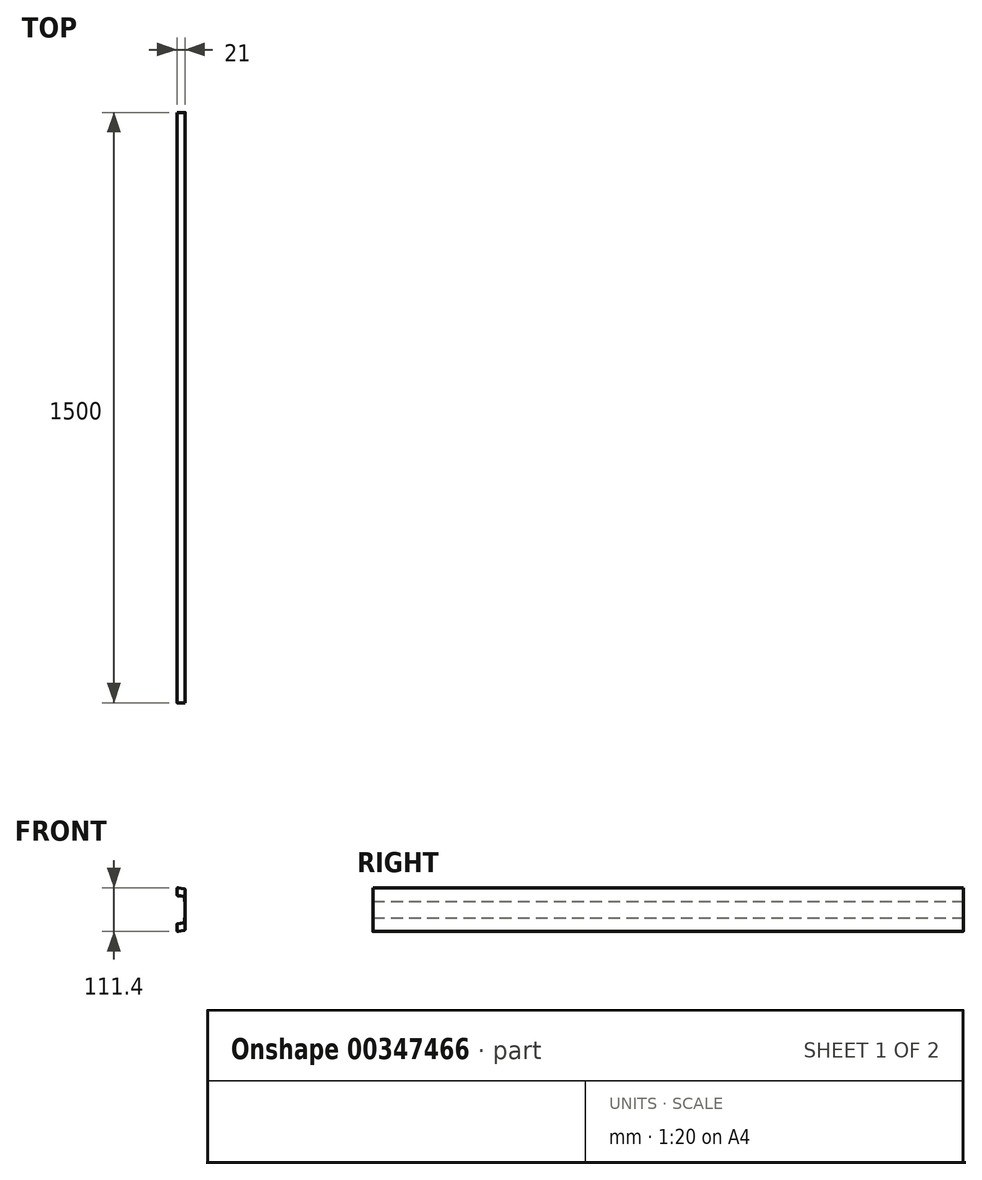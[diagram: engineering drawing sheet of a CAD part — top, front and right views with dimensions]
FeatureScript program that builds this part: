
annotation { "Feature Type Name" : "Feature", "Feature Type Description" : "" }
export const myFeature = defineFeature(function(context is Context, id is Id, definition is map)
    precondition{}
    {
        {
            var Q0;
            Q0=qCreatedBy(makeId("Front.planeOp"),FACE);
            var sketch = newSketch(context, id + "F0", { "sketchPlane" : qUnion([Q0])});
            skLineSegment(sketch, "E0", {"start": v(-1.5, -20.57) * mm, "end": v(-1.5, -32.53) * mm});
            skLineSegment(sketch, "E1", {"start": v(-1.5, -32.53) * mm, "end": v(-21, -35.97) * mm});
            skLineSegment(sketch, "E2", {"start": v(-21, -35.97) * mm, "end": v(-21, -56.27) * mm});
            skLineSegment(sketch, "E3", {"start": v(-21, -56.27) * mm, "end": v(0, -52.57) * mm});
            skLineSegment(sketch, "E4", {"start": v(0, -52.57) * mm, "end": v(0, 52.57) * mm});
            skLineSegment(sketch, "E5", {"start": v(0, 52.57) * mm, "end": v(-21, 56.27) * mm});
            skLineSegment(sketch, "E6", {"start": v(-21, 56.27) * mm, "end": v(-21, 35.97) * mm});
            skLineSegment(sketch, "E7", {"start": v(-21, 35.97) * mm, "end": v(-1.5, 32.53) * mm});
            skLineSegment(sketch, "E8", {"start": v(-1.5, 32.53) * mm, "end": v(-1.5, 20.57) * mm});
            skLineSegment(sketch, "E9.0", {"start": v(-1, 32.95) * mm, "end": v(-1, 20.57) * mm});
            skLineSegment(sketch, "E10.0", {"start": v(-20.5, 36.39) * mm, "end": v(-1, 32.95) * mm});
            skLineSegment(sketch, "E11.0", {"start": v(-20.5, 55.68) * mm, "end": v(-20.5, 36.39) * mm});
            skLineSegment(sketch, "E12.0", {"start": v(-0.5, 52.15) * mm, "end": v(-20.5, 55.68) * mm});
            skLineSegment(sketch, "E13.0", {"start": v(-0.5, -52.15) * mm, "end": v(-0.5, 52.15) * mm});
            skLineSegment(sketch, "E14.0", {"start": v(-20.5, -55.68) * mm, "end": v(-0.5, -52.15) * mm});
            skLineSegment(sketch, "E15.0", {"start": v(-20.5, -36.39) * mm, "end": v(-20.5, -55.68) * mm});
            skLineSegment(sketch, "E16.0", {"start": v(-1, -32.95) * mm, "end": v(-20.5, -36.39) * mm});
            skLineSegment(sketch, "E17.0", {"start": v(-1, -20.57) * mm, "end": v(-1, -32.95) * mm});
            skLineSegment(sketch, "E18", {"start": v(-1.5, 20.57) * mm, "end": v(-1, 20.57) * mm});
            skLineSegment(sketch, "E19", {"start": v(-1.5, -20.57) * mm, "end": v(-1, -20.57) * mm});
            skSolve(sketch);
        }
        {
            var Q0;
            Q0=makeQuery(id+"F0.imprint","IMPRINT",FACE,{"disambiguationData":[TD([[makeQuery(id+"F0.imprint","IMPRINT",EDGE,{"derivedFrom":sQuery(id+"F0.wireOp",EDGE,"E0")}),1.0]])]});
            extrude(context, id + "F1", {"entities" : qUnion([Q0]), "endBound" : BoundingType.SYMMETRIC, "depth" : 1500 * mm});
        }
        {
            var Q0;
            Q0=makeQuery(id+"F1.opExtrude","SWEPT_EDGE",EDGE,{"disambiguationData":[OSD([sQuery(id+"F0.wireOp",EDGE,"E12.0"),sQuery(id+"F0.wireOp",EDGE,"E13.0")])]});
            var Q1;
            Q1=makeQuery(id+"F1.opExtrude","SWEPT_EDGE",EDGE,{"disambiguationData":[OSD([sQuery(id+"F0.wireOp",EDGE,"E10.0"),sQuery(id+"F0.wireOp",EDGE,"E11.0")])]});
            var Q2;
            Q2=makeQuery(id+"F1.opExtrude","SWEPT_EDGE",EDGE,{"disambiguationData":[OSD([sQuery(id+"F0.wireOp",EDGE,"E11.0"),sQuery(id+"F0.wireOp",EDGE,"E12.0")])]});
            var Q3;
            Q3=makeQuery(id+"F1.opExtrude","SWEPT_EDGE",EDGE,{"disambiguationData":[OSD([sQuery(id+"F0.wireOp",EDGE,"E15.0"),sQuery(id+"F0.wireOp",EDGE,"E16.0")])]});
            var Q4;
            Q4=makeQuery(id+"F1.opExtrude","SWEPT_EDGE",EDGE,{"disambiguationData":[OSD([sQuery(id+"F0.wireOp",EDGE,"E13.0"),sQuery(id+"F0.wireOp",EDGE,"E14.0")])]});
            var Q5;
            Q5=makeQuery(id+"F1.opExtrude","SWEPT_EDGE",EDGE,{"disambiguationData":[OSD([sQuery(id+"F0.wireOp",EDGE,"E14.0"),sQuery(id+"F0.wireOp",EDGE,"E15.0")])]});
            fillet(context, id + "F2", {"entities" : qUnion([Q0, Q1, Q2, Q3, Q4, Q5]), "radius" : 2.5 * mm, "tangentPropagation" : true, "allowEdgeOverflow" : false});
        }
        {
            var Q0;
            Q0=makeQuery(id+"F1.opExtrude","SWEPT_EDGE",EDGE,{"disambiguationData":[OSD([sQuery(id+"F0.wireOp",EDGE,"E4"),sQuery(id+"F0.wireOp",EDGE,"E5")])]});
            var Q1;
            Q1=makeQuery(id+"F1.opExtrude","SWEPT_EDGE",EDGE,{"disambiguationData":[OSD([sQuery(id+"F0.wireOp",EDGE,"E6"),sQuery(id+"F0.wireOp",EDGE,"E7")])]});
            var Q2;
            Q2=makeQuery(id+"F1.opExtrude","SWEPT_EDGE",EDGE,{"disambiguationData":[OSD([sQuery(id+"F0.wireOp",EDGE,"E5"),sQuery(id+"F0.wireOp",EDGE,"E6")])]});
            var Q3;
            Q3=makeQuery(id+"F1.opExtrude","SWEPT_EDGE",EDGE,{"disambiguationData":[OSD([sQuery(id+"F0.wireOp",EDGE,"E1"),sQuery(id+"F0.wireOp",EDGE,"E2")])]});
            var Q4;
            Q4=makeQuery(id+"F1.opExtrude","SWEPT_EDGE",EDGE,{"disambiguationData":[OSD([sQuery(id+"F0.wireOp",EDGE,"E2"),sQuery(id+"F0.wireOp",EDGE,"E3")])]});
            var Q5;
            Q5=makeQuery(id+"F1.opExtrude","SWEPT_EDGE",EDGE,{"disambiguationData":[OSD([sQuery(id+"F0.wireOp",EDGE,"E3"),sQuery(id+"F0.wireOp",EDGE,"E4")])]});
            fillet(context, id + "F3", {"entities" : qUnion([Q0, Q1, Q2, Q3, Q4, Q5]), "radius" : 3 * mm, "tangentPropagation" : true, "allowEdgeOverflow" : false});
        }
        {
            var Q0;
            Q0=makeQuery(id+"F1.opExtrude","SWEPT_EDGE",EDGE,{"disambiguationData":[OSD([sQuery(id+"F0.wireOp",EDGE,"E7"),sQuery(id+"F0.wireOp",EDGE,"E8")])]});
            var Q1;
            Q1=makeQuery(id+"F1.opExtrude","SWEPT_EDGE",EDGE,{"disambiguationData":[OSD([sQuery(id+"F0.wireOp",EDGE,"E0"),sQuery(id+"F0.wireOp",EDGE,"E1")])]});
            fillet(context, id + "F4", {"entities" : qUnion([Q0, Q1]), "radius" : 5 * mm, "tangentPropagation" : true, "allowEdgeOverflow" : false});
        }
        {
            var Q0;
            Q0=makeQuery(id+"F1.opExtrude","SWEPT_EDGE",EDGE,{"disambiguationData":[OSD([sQuery(id+"F0.wireOp",EDGE,"E16.0"),sQuery(id+"F0.wireOp",EDGE,"E17.0")])]});
            var Q1;
            Q1=makeQuery(id+"F1.opExtrude","SWEPT_EDGE",EDGE,{"disambiguationData":[OSD([sQuery(id+"F0.wireOp",EDGE,"E9.0"),sQuery(id+"F0.wireOp",EDGE,"E10.0")])]});
            fillet(context, id + "F5", {"entities" : qUnion([Q0, Q1]), "radius" : 5.5 * mm, "tangentPropagation" : true, "allowEdgeOverflow" : false});
        }
    });
